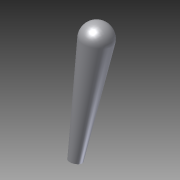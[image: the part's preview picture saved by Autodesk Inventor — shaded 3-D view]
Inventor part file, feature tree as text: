
AUTODESK INVENTOR PART (.ipt)
format: ipt  version: 2011 SP1 (Build 150282100, 282)  size: 92,160 bytes
history: native  units: in
note: dims shown in document units (in); Inventor stores cm internally (conversion verified against a paired STEP export)
features: other x14, revolve x1, sketch x1
ambient origin geometry x8: Origin, YZ Plane, XZ Plane, XY Plane, X Axis, Y Axis, Z Axis, Center Point
bodies: Solid1 (feature_tree)
feature tree (16):
  revolve  "Revolution1"  [1 undecoded]
  other  "toggle_XY"
  other  "toggle_YZ"
  other  "toggle_ZX"
  other  "toggle_X"
  other  "toggle_Y"
  other  "toggle_Z"
  other  "toggle_Center"
  other  "toggle_cap_XY"
  other  "toggle_cap_YZ"
  other  "toggle_cap_ZX"
  other  "toggle_cap_X"
  other  "toggle_cap_Y"
  other  "toggle_cap_Z"
  other  "toggle_cap_Center"
  sketch  "Sketch_1"  dims[d0=360.0deg]
note: 1 required parameter value undecoded (feature->parameter linkage not recoverable at this tier; creation-order binding heuristic only, values carry confidence <= 0.55)
